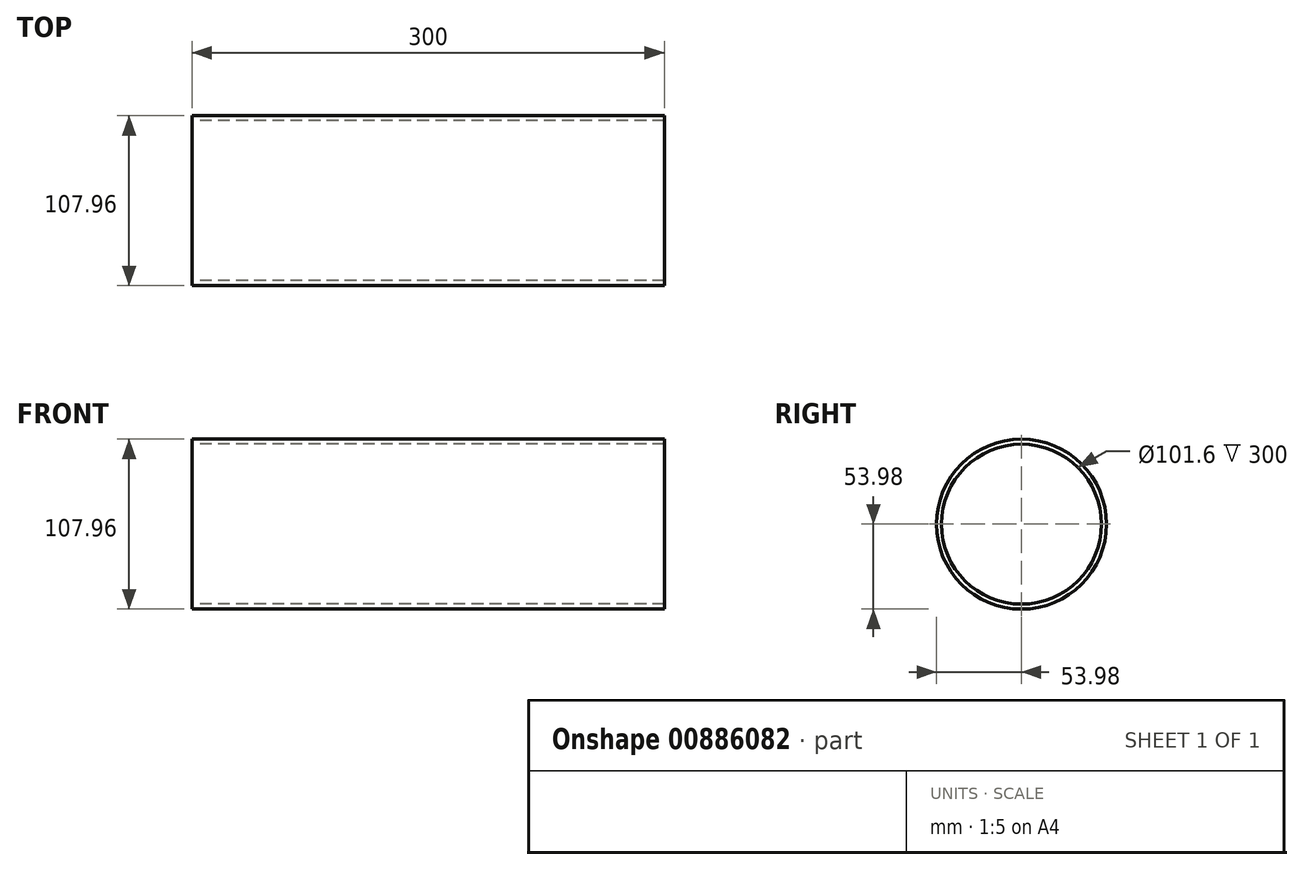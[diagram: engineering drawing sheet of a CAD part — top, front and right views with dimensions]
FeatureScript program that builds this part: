
annotation { "Feature Type Name" : "Feature", "Feature Type Description" : "" }
export const myFeature = defineFeature(function(context is Context, id is Id, definition is map)
    precondition{}
    {
        {
            var Q0;
            Q0=qCreatedBy(makeId("Right.planeOp"),FACE);
            var sketch = newSketch(context, id + "F0", { "sketchPlane" : qUnion([Q0])});
            skCircle(sketch, "E0", {"center": v(0, 0) * mm, "radius": 50.8 * mm});
            skCircle(sketch, "E1", {"center": v(0, 0) * mm, "radius": 53.98 * mm});
            skSolve(sketch);
        }
        {
            var Q0;
            Q0=qSketchRegion(id+"F0",true);
            extrude(context, id + "F1", {"entities" : qUnion([Q0]), "depth" : 300 * mm, "offsetDistance" : 25 * mm});
        }
    });
